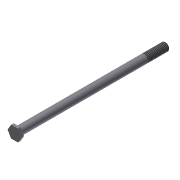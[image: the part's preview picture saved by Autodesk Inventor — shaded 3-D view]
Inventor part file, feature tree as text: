
AUTODESK INVENTOR PART (.ipt)
format: ipt  version: 2011 (Build 150239000, 239)  size: 85,504 bytes
history: native  units: in
note: dims shown in document units (in); Inventor stores cm internally (conversion verified against a paired STEP export)
features: extrude x2, sketch x2, thread x1, chamfer x1
ambient origin geometry x8: Origin, YZ Plane, XZ Plane, XY Plane, X Axis, Y Axis, Z Axis, Center Point
bodies: Solid1 (feature_tree)
feature tree (6):
  extrude  "Extrusion1"  Depth=7.0in TaperAngle=0.0deg
  extrude  "Extrusion2"  Depth=0.125in TaperAngle=0.0deg
  thread  "Thread1"  [1 undecoded]
  chamfer  "Chamfer1"  Distance=0.02in Angle=45.0deg
  sketch  "Sketch1"  dims[d0=0.375in d1=7.0in d2=0.0in]
  sketch  "Sketch2"  dims[d3=0.5625in d4=0.125in d5=0.0in d6=1.0in d7=0.0in d8=0.02in d9=0.125in d10=45.0deg]
note: 1 required parameter value undecoded (feature->parameter linkage not recoverable at this tier; creation-order binding heuristic only, values carry confidence <= 0.55)
